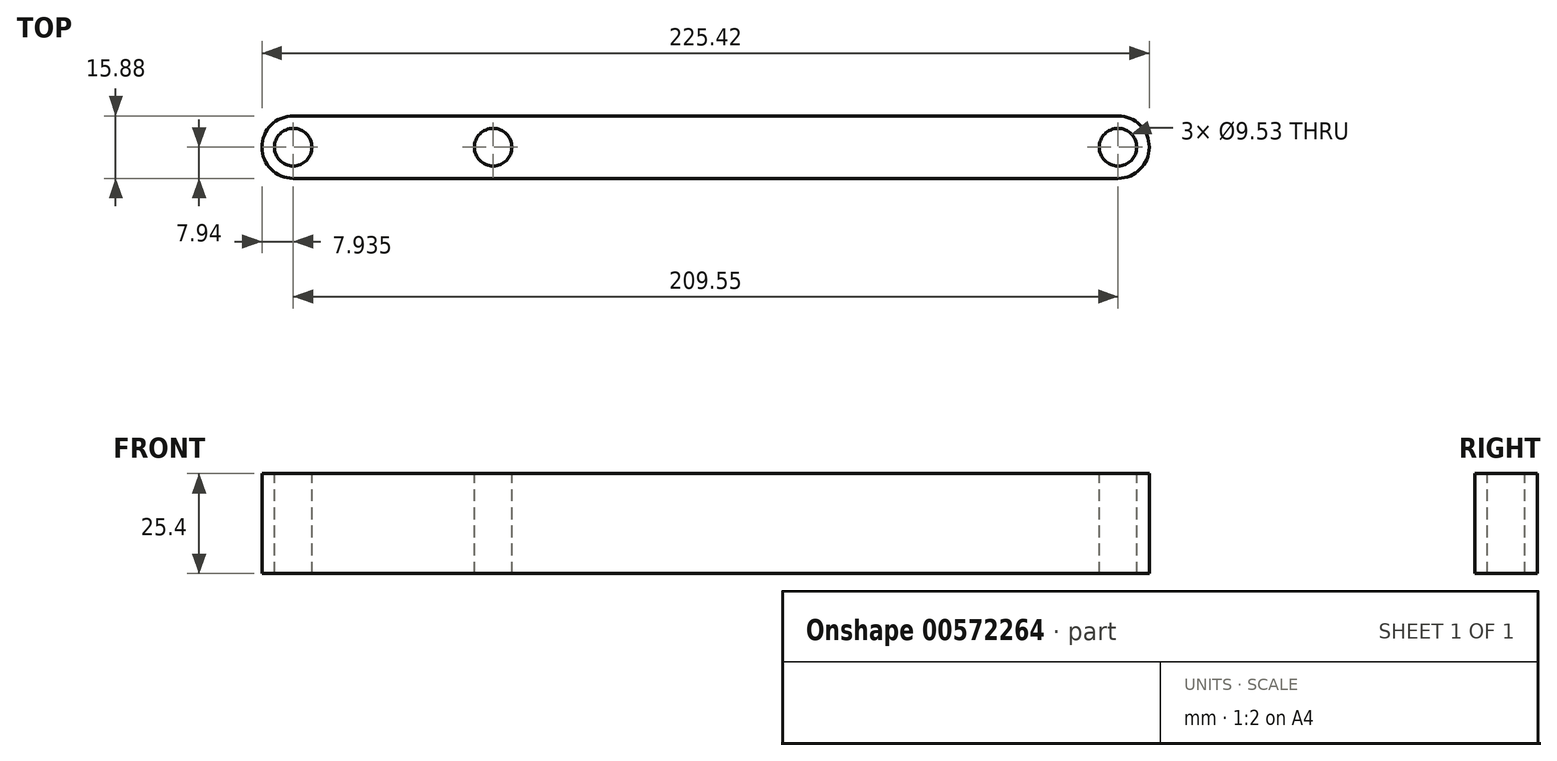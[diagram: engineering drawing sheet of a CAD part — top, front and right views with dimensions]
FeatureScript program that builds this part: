
annotation { "Feature Type Name" : "Feature", "Feature Type Description" : "" }
export const myFeature = defineFeature(function(context is Context, id is Id, definition is map)
    precondition{}
    {
        {
            var Q0;
            Q0=qCreatedBy(makeId("Top.planeOp"),FACE);
            var sketch = newSketch(context, id + "F0", { "sketchPlane" : qUnion([Q0])});
            skLineSegment(sketch, "E0.bottom", {"start": v(-112.71, 7.94) * mm, "end": v(112.71, 7.94) * mm});
            skLineSegment(sketch, "E0.top", {"start": v(-112.71, -7.94) * mm, "end": v(112.71, -7.94) * mm});
            skLineSegment(sketch, "E0.left", {"start": v(-112.71, 7.94) * mm, "end": v(-112.71, -7.94) * mm});
            skLineSegment(sketch, "E0.right", {"start": v(112.71, 7.94) * mm, "end": v(112.71, -7.94) * mm});
            skSolve(sketch);
        }
        {
            var Q0;
            Q0=makeQuery(id+"F0.imprint","IMPRINT",FACE,{"disambiguationData":[TD([[makeQuery(id+"F0.imprint","IMPRINT",EDGE,{"derivedFrom":sQuery(id+"F0.wireOp",EDGE,"E0.bottom")}),-1.0]])]});
            extrude(context, id + "F1", {"entities" : qUnion([Q0]), "depth" : 25.4 * mm, "offsetDistance" : 25.4 * mm});
        }
        {
            var Q0;
            Q0=makeQuery(id+"F1.opExtrude","CAP_FACE",FACE,{"disambiguationData":[OSD([sQuery(id+"F0.wireOp",EDGE,"E0.bottom"),sQuery(id+"F0.wireOp",EDGE,"E0.top"),sQuery(id+"F0.wireOp",EDGE,"E0.left"),sQuery(id+"F0.wireOp",EDGE,"E0.right")])],"isStart":false});
            var sketch = newSketch(context, id + "F2", { "sketchPlane" : qUnion([Q0])});
            skPoint(sketch, "E1", {"position": v(-104.78, 0) * mm});
            skPoint(sketch, "E2", {"position": v(104.78, 0) * mm});
            skPoint(sketch, "E3", {"position": v(-53.98, 0) * mm});
            skSolve(sketch);
        }
        {
            var Q0;
            Q0=sQuery(id+"F2.wireOp",VERTEX,"E2");
            var Q1;
            Q1=sQuery(id+"F2.wireOp",VERTEX,"E1");
            var Q2;
            Q2=sQuery(id+"F2.wireOp",VERTEX,"E3");
            var Q3;
            Q3=makeQuery(id+"F1.opExtrude","SWEPT_BODY",BODY,{"disambiguationData":[OSD([sQuery(id+"F0.wireOp",EDGE,"E0.bottom"),sQuery(id+"F0.wireOp",EDGE,"E0.top"),sQuery(id+"F0.wireOp",EDGE,"E0.left"),sQuery(id+"F0.wireOp",EDGE,"E0.right")])]});
            hole(context, id + "F3", {"style" : HoleStyle.SIMPLE, "endStyle" : HoleEndStyle.THROUGH, "holeDiameter" : 9.52 * mm, "isTappedThrough" : true, "tappedDepth" : 12.7 * mm, "tapClearance" : 3, "locations" : qUnion([Q0, Q1, Q2]), "scope" : qUnion([Q3])});
        }
        {
            var Q0;
            Q0=makeQuery(id+"F1.opExtrude","SWEPT_EDGE",EDGE,{"disambiguationData":[OSD([sQuery(id+"F0.wireOp",EDGE,"E0.top"),sQuery(id+"F0.wireOp",EDGE,"E0.left")])]});
            var Q1;
            Q1=makeQuery(id+"F1.opExtrude","SWEPT_EDGE",EDGE,{"disambiguationData":[OSD([sQuery(id+"F0.wireOp",EDGE,"E0.top"),sQuery(id+"F0.wireOp",EDGE,"E0.right")])]});
            var Q2;
            Q2=makeQuery(id+"F1.opExtrude","SWEPT_EDGE",EDGE,{"disambiguationData":[OSD([sQuery(id+"F0.wireOp",EDGE,"E0.bottom"),sQuery(id+"F0.wireOp",EDGE,"E0.right")])]});
            var Q3;
            Q3=makeQuery(id+"F1.opExtrude","SWEPT_EDGE",EDGE,{"disambiguationData":[OSD([sQuery(id+"F0.wireOp",EDGE,"E0.bottom"),sQuery(id+"F0.wireOp",EDGE,"E0.left")])]});
            fillet(context, id + "F4", {"entities" : qUnion([Q0, Q1, Q2, Q3]), "radius" : 7.94 * mm, "tangentPropagation" : true, "allowEdgeOverflow" : false});
        }
    });
